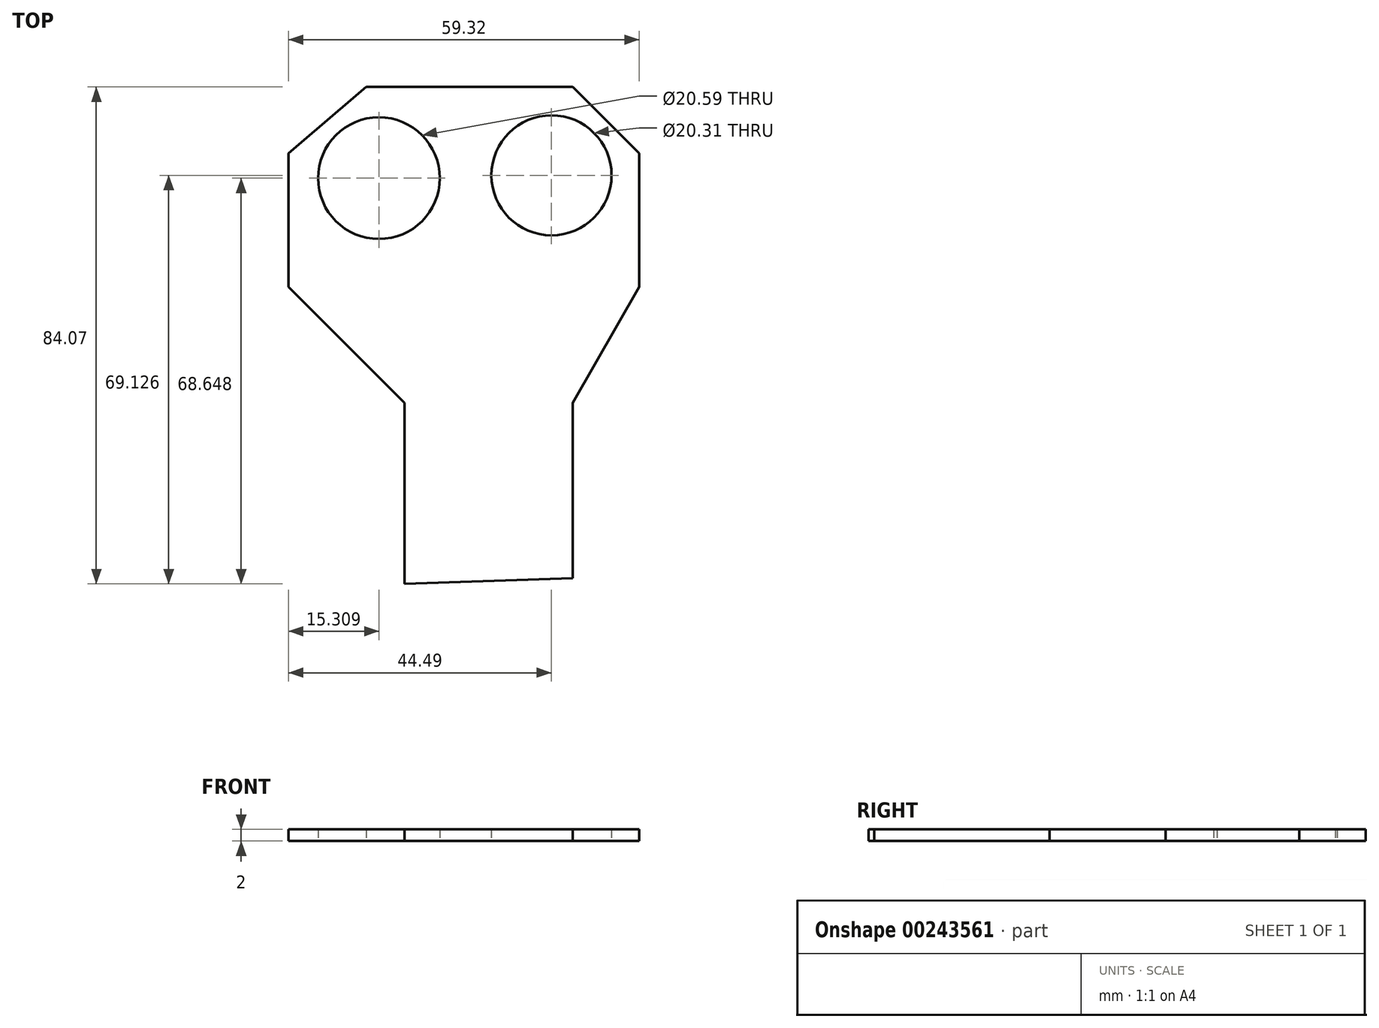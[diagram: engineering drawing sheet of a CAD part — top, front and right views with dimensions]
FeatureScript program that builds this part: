
annotation { "Feature Type Name" : "Feature", "Feature Type Description" : "" }
export const myFeature = defineFeature(function(context is Context, id is Id, definition is map)
    precondition{}
    {
        {
            var Q0;
            Q0=qCreatedBy(makeId("Top.planeOp"),FACE);
            var sketch = newSketch(context, id + "F0", { "sketchPlane" : qUnion([Q0])});
            skLineSegment(sketch, "E0", {"start": v(-24.88, -53.22) * mm, "end": v(-24.88, -22.6) * mm});
            skLineSegment(sketch, "E1", {"start": v(-24.88, -22.6) * mm, "end": v(-44.49, -2.99) * mm});
            skLineSegment(sketch, "E2", {"start": v(-44.49, -2.99) * mm, "end": v(-44.49, 19.61) * mm});
            skLineSegment(sketch, "E3", {"start": v(-44.49, 19.61) * mm, "end": v(-31.33, 30.85) * mm});
            skLineSegment(sketch, "E4", {"start": v(-31.33, 30.85) * mm, "end": v(3.59, 30.85) * mm});
            skLineSegment(sketch, "E5", {"start": v(3.59, 30.85) * mm, "end": v(14.83, 19.61) * mm});
            skLineSegment(sketch, "E6", {"start": v(14.83, 19.61) * mm, "end": v(14.83, -2.99) * mm});
            skLineSegment(sketch, "E7", {"start": v(14.83, -2.99) * mm, "end": v(3.59, -22.6) * mm});
            skLineSegment(sketch, "E8", {"start": v(3.59, -22.6) * mm, "end": v(3.59, -52.26) * mm});
            skLineSegment(sketch, "E9", {"start": v(3.59, -52.26) * mm, "end": v(-24.88, -53.22) * mm});
            skCircle(sketch, "E10", {"center": v(-29.18, 15.43) * mm, "radius": 10.3 * mm});
            skCircle(sketch, "E11", {"center": v(0, 15.9) * mm, "radius": 10.15 * mm});
            skSolve(sketch);
        }
        {
            var Q0;
            Q0=makeQuery(id+"F0.imprint","IMPRINT",FACE,{"disambiguationData":[TD([[makeQuery(id+"F0.imprint","IMPRINT",EDGE,{"derivedFrom":sQuery(id+"F0.wireOp",EDGE,"E0")}),-1.0]])]});
            extrude(context, id + "F1", {"entities" : qUnion([Q0]), "depth" : 2 * mm});
        }
    });
